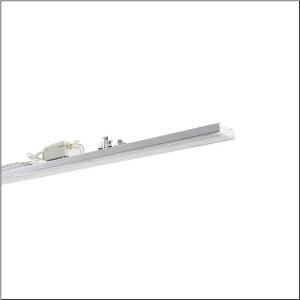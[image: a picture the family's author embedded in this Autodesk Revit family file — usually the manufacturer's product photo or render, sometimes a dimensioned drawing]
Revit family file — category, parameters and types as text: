
# Revit family: licross_r__21_recessed_ho_52tl1edv4l2s_3d33
name_source: partatom
category: Lighting Fixtures
units: mm (PartAtom-declared; Revit-internal decimal feet)

## family parameters
Cut with Voids When Loaded = No
Host = Face
Light Source = No
Part Type = Normal
Room Calculation Point = No
Round Connector Dimension = Use Diameter
Shared = No

## types (1)
- --- (1 x LED, 22130 lm, 125.6 W, 4000K)
    Apparent Load = 126 VA
    CIE Flux Codes = 85 95 99 100 100
    Color Rendering = 80
    Color Temperature = 4000K
    Default Elevation = 1800 mm
    Description = Licross® 21 Recessed HO, luminaire insert, of sheet steel, galvanised, coil coated, white, length: 2.250mm, width: 66mm, height: 67mm, LED rated luminous flux: 22.130lm, light colour: 840, control gear: DALI 2, with plug, 5-pole, with phase selection, mains connection: 220..240V, AC, 50/60Hz, rated input power: 126W, halogen-free wiring, primary light control with lens, of plastic, primary optical cover: cover, of PMMA, light emission: direct distribution, primary light characteristic: symmetric, protection rating (complete): IP40, insulation class (complete): insulation class I (protective earthing), certification: CE, ENEC, VDE, UKCA, protection symbol: D if used in an environment without relevant dust loads with corresponding accessories, impact resistance: IK06, permissible ambient temperature for indoor applications: -40..+30°C, corresponds to IFS (International Featured Standards) requirements for safety and quality in the food industry, reducing of maximum allowable ambient temperature of 5°C with ceiling mounting, LABS conformity tested according to VDMA 24364:2018-05, packaging unit: 1 piece
    Height = 58 mm
    Lamp = 1 x LED
    Lamp Light Flux = 22130 lm
    Lamp Power = 125.6 W
    Lamp count = 1
    Length = 2250 mm
    Luminous efficacy = 176 lm/W
    Manufacturer = Siteco
    ModVariant = No
    Model = 52TL1EDV4L2S
    Mounting Place = Ceiling
    Mounting Type = Pendant
    Number of Poles = 1
    OnlyDefault = Yes
    Power Factor = 1
    Product Name = Licross® 21 Recessed HO
    Product group = luminaire insert
    ProductGroupID = 901
    Protection Class = Protection class I
    Protection Degree = IP 40
    RLX_Detail_Level = 1
    RLX_Emergency_Light_Flux = 0 lm
    RLX_Emergency_Type = 0
    RLX_Emergency_Type_DB = No
    RlxData = <blob elided: 29685 chars, md5=e93e022e>
    Socket = socket
    Standby Power = 0 W
    System Light Flux = 22129 lm
    System Power = 126 W
    Type Comments = factory setting: luminous flux: 100 % | dim-lin: 254 | 489 mA
    Type Image = l_1296930.jpg
    URL = http://relux.com
    VarID = @adj_057083
    Voltage = 0 V
    Weight = 0.00 kg
    Width = 66 mm

## geometry (parser evidence)
native form markers: Blend x4, Sweep x11
no freeform markers — native parametric forms only
